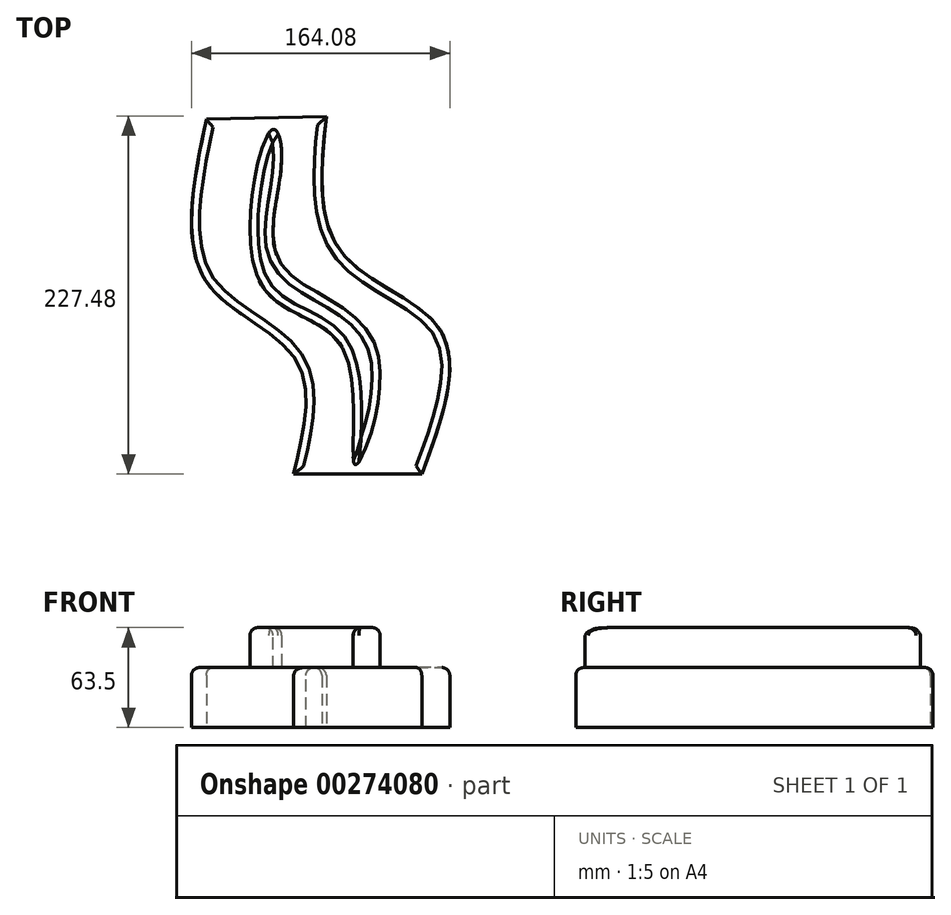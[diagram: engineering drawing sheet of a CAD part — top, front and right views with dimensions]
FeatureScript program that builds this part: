
annotation { "Feature Type Name" : "Feature", "Feature Type Description" : "" }
export const myFeature = defineFeature(function(context is Context, id is Id, definition is map)
    precondition{}
    {
        {
            var Q0;
            Q0=qCreatedBy(makeId("Top.planeOp"),FACE);
            var sketch = newSketch(context, id + "F0", { "sketchPlane" : qUnion([Q0])});
            skFitSpline(sketch, "E0", {"points": [v(-50.66, 77.38) * mm, v(-51.45, 11.17) * mm, v(9.17, -42.28) * mm, v(-3.99, -116.87) * mm, v(-11.57, -43.88) * mm, v(-65.02, 0) * mm, v(-57.04, 95.73) * mm, v(-50.66, 77.38) * mm]});
            skFitSpline(sketch, "E1", {"points": [v(-22.34, 104.1) * mm, v(-12.36, 17.55) * mm, v(50.66, -32.3) * mm, v(38.3, -122.85) * mm], "startDerivative": vector(-30.48, -293.5) * mm, "endDerivative": vector(-110.8, -300.68) * mm});
            skFitSpline(sketch, "E2", {"points": [v(-98.52, 102.5) * mm, v(-98.92, 0) * mm, v(-41.88, -49.86) * mm, v(-43.08, -122.85) * mm], "startDerivative": vector(-65.8, -317.05) * mm, "endDerivative": vector(-63, -261.43) * mm});
            skLineSegment(sketch, "E3", {"start": v(-98.52, 102.5) * mm, "end": v(-22.34, 104.1) * mm});
            skLineSegment(sketch, "E4", {"start": v(-43.08, -122.85) * mm, "end": v(38.3, -122.85) * mm});
            skSolve(sketch);
        }
        {
            var Q0;
            Q0=makeQuery(id+"F0.imprint","IMPRINT",FACE,{"disambiguationData":[TD([[makeQuery(id+"F0.imprint","IMPRINT",EDGE,{"derivedFrom":sQuery(id+"F0.wireOp",EDGE,"E0")}),-1.0]])]});
            extrude(context, id + "F1", {"entities" : qUnion([Q0]), "depth" : 63.5 * mm});
        }
        {
            var Q0;
            Q0=makeQuery(id+"F0.imprint","IMPRINT",FACE,{"disambiguationData":[TD([[makeQuery(id+"F0.imprint","IMPRINT",EDGE,{"derivedFrom":sQuery(id+"F0.wireOp",EDGE,"E0")}),1.0]])]});
            extrude(context, id + "F2", {"entities" : qUnion([Q0]), "operationType" : NewBodyOperationType.ADD, "depth" : 38.1 * mm});
        }
        {
            var Q0;
            Q0=makeQuery(id+"F2.opExtrude","CAP_EDGE",EDGE,{"disambiguationData":[OSD([sQuery(id+"F0.wireOp",EDGE,"E1")])],"isStart":false});
            var Q1;
            Q1=makeQuery(id+"F2.opExtrude","CAP_EDGE",EDGE,{"disambiguationData":[OSD([sQuery(id+"F0.wireOp",EDGE,"E4")])],"isStart":false});
            var Q2;
            Q2=makeQuery(id+"F2.opExtrude","CAP_EDGE",EDGE,{"disambiguationData":[OSD([sQuery(id+"F0.wireOp",EDGE,"E2")])],"isStart":false});
            var Q3;
            Q3=makeQuery(id+"F2.opExtrude","CAP_EDGE",EDGE,{"disambiguationData":[OSD([sQuery(id+"F0.wireOp",EDGE,"E3")])],"isStart":false});
            var Q4;
            Q4=makeQuery(id+"F1.opExtrude","CAP_EDGE",EDGE,{"disambiguationData":[OSD([sQuery(id+"F0.wireOp",EDGE,"E0")])],"isStart":false});
            fillet(context, id + "F3", {"entities" : qUnion([Q0, Q1, Q2, Q3, Q4]), "radius" : 5.08 * mm, "tangentPropagation" : true, "allowEdgeOverflow" : false});
        }
    });
